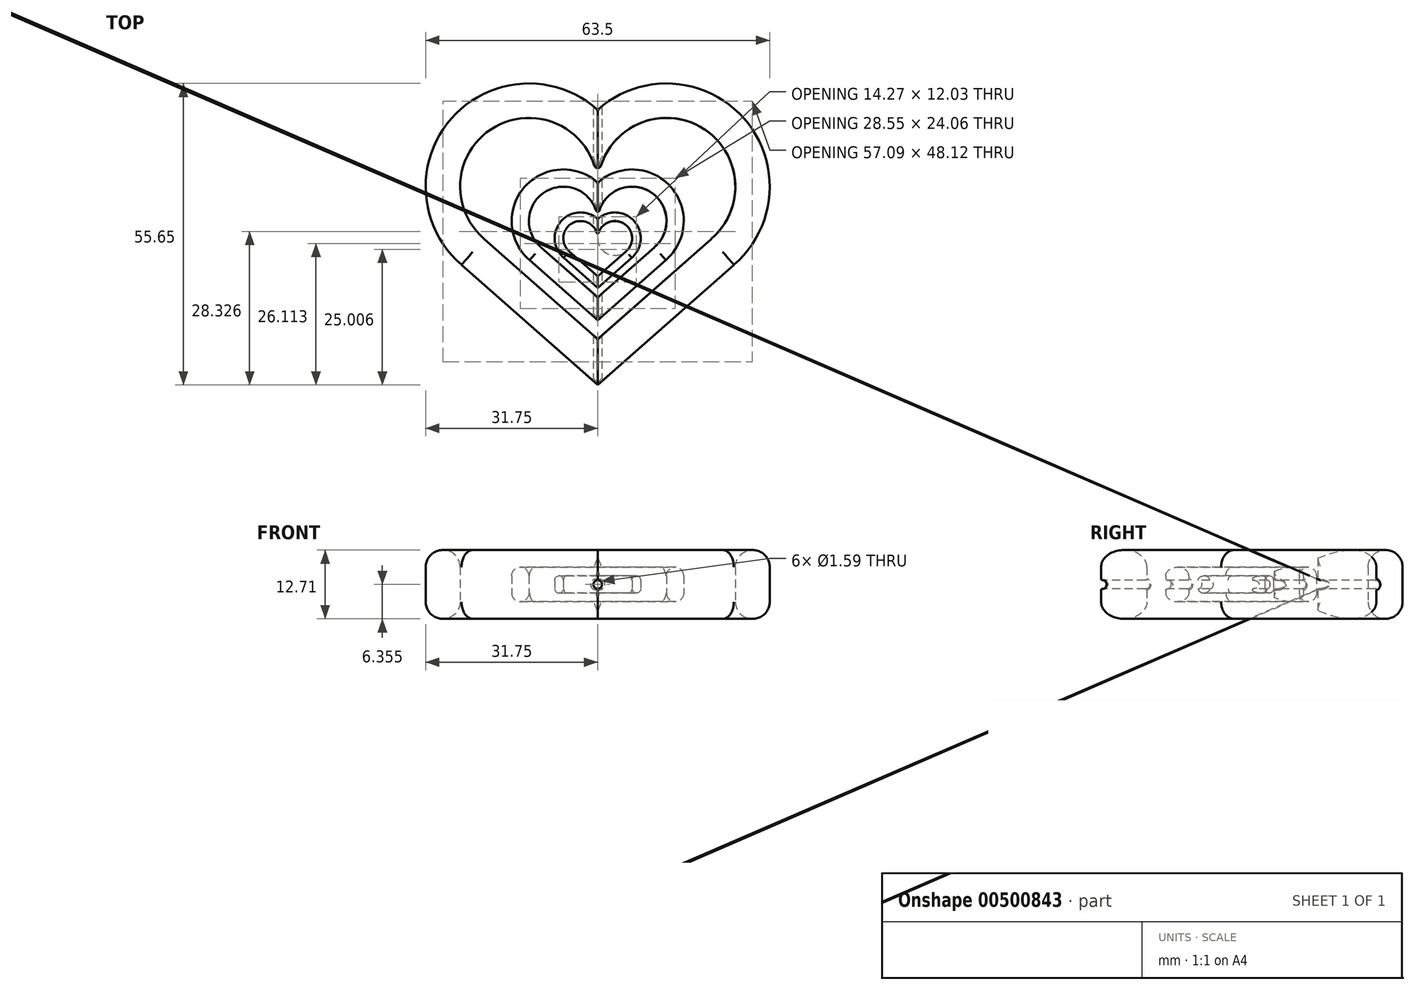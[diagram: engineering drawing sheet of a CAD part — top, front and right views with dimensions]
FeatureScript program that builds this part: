
annotation { "Feature Type Name" : "Feature", "Feature Type Description" : "" }
export const myFeature = defineFeature(function(context is Context, id is Id, definition is map)
    precondition{}
    {
        {
            var Q0;
            Q0=qCreatedBy(makeId("Top.planeOp"),FACE);
            var sketch = newSketch(context, id + "F0", { "sketchPlane" : qUnion([Q0])});
            skArc(sketch, "E0", {"start": v(0, 7.1) * mm, "mid": v(-13.5, 6.29) * mm, "end": v(-12.57, -7.21) * mm});
            skArc(sketch, "E1", {"start": v(0, 7.1) * mm, "mid": v(13.5, 6.29) * mm, "end": v(12.57, -7.21) * mm});
            skLineSegment(sketch, "E2", {"start": v(-12.57, -7.21) * mm, "end": v(0, -18.3) * mm});
            skLineSegment(sketch, "E3", {"start": v(0, -18.3) * mm, "end": v(12.57, -7.21) * mm});
            skArc(sketch, "E4", {"start": v(0, 0) * mm, "mid": v(-9, 5.77) * mm, "end": v(-10.5, -4.8) * mm});
            skArc(sketch, "E5", {"start": v(0, 0) * mm, "mid": v(9, 5.77) * mm, "end": v(10.49, -4.82) * mm});
            skLineSegment(sketch, "E6", {"start": v(10.49, -4.82) * mm, "end": v(0, -14.07) * mm});
            skLineSegment(sketch, "E7", {"start": v(0, -14.07) * mm, "end": v(-10.47, -4.83) * mm});
            skLineSegment(sketch, "E8", {"start": v(-10.47, -4.83) * mm, "end": v(-10.5, -4.8) * mm});
            skSolve(sketch);
        }
        {
            var Q0;
            Q0=makeQuery(id+"F0.imprint","IMPRINT",FACE,{"disambiguationData":[TD([[makeQuery(id+"F0.imprint","IMPRINT",EDGE,{"derivedFrom":sQuery(id+"F0.wireOp",EDGE,"E0")}),1.0]])]});
            extrude(context, id + "F1", {"entities" : qUnion([Q0]), "depth" : 6.35 * mm});
        }
        {
            var Q0;
            Q0=makeQuery(id+"F1.opExtrude","CAP_FACE",FACE,{"disambiguationData":[OSD([sQuery(id+"F0.wireOp",EDGE,"E0"),sQuery(id+"F0.wireOp",EDGE,"E1"),sQuery(id+"F0.wireOp",EDGE,"E2"),sQuery(id+"F0.wireOp",EDGE,"E3")])],"isStart":false});
            var Q1;
            Q1=makeQuery(id+"F1.opExtrude","CAP_FACE",FACE,{"disambiguationData":[OSD([sQuery(id+"F0.wireOp",EDGE,"E0"),sQuery(id+"F0.wireOp",EDGE,"E1"),sQuery(id+"F0.wireOp",EDGE,"E2"),sQuery(id+"F0.wireOp",EDGE,"E3")])],"isStart":true});
            fillet(context, id + "F2", {"entities" : qUnion([Q0, Q1]), "radius" : 1.57 * mm, "tangentPropagation" : true, "allowEdgeOverflow" : false});
        }
        {
            var Q0;
            Q0=makeQuery(id+"F2.opFillet","BLEND_EDGE",EDGE,{"blendedFrom":[makeQuery(id+"F1.opExtrude","CAP_EDGE",EDGE,{"disambiguationData":[OSD([sQuery(id+"F0.wireOp",EDGE,"E0")])],"isStart":false}),makeQuery(id+"F1.opExtrude","CAP_EDGE",EDGE,{"disambiguationData":[OSD([sQuery(id+"F0.wireOp",EDGE,"E2")])],"isStart":false})],"blendedInto":[]});
            var Q1;
            Q1=makeQuery(id+"F2.opFillet","BLEND_EDGE",EDGE,{"blendedFrom":[makeQuery(id+"F1.opExtrude","CAP_EDGE",EDGE,{"disambiguationData":[OSD([sQuery(id+"F0.wireOp",EDGE,"E1")])],"isStart":false}),makeQuery(id+"F1.opExtrude","CAP_EDGE",EDGE,{"disambiguationData":[OSD([sQuery(id+"F0.wireOp",EDGE,"E3")])],"isStart":false})],"blendedInto":[]});
            var Q2;
            Q2=makeQuery(id+"F1.opExtrude","SWEPT_EDGE",EDGE,{"disambiguationData":[OSD([sQuery(id+"F0.wireOp",EDGE,"E0"),sQuery(id+"F0.wireOp",EDGE,"E2")])]});
            var Q3;
            Q3=makeQuery(id+"F1.opExtrude","SWEPT_EDGE",EDGE,{"disambiguationData":[OSD([sQuery(id+"F0.wireOp",EDGE,"E1"),sQuery(id+"F0.wireOp",EDGE,"E3")])]});
            var Q4;
            Q4=makeQuery(id+"F2.opFillet","BLEND_EDGE",EDGE,{"blendedFrom":[makeQuery(id+"F1.opExtrude","CAP_EDGE",EDGE,{"disambiguationData":[OSD([sQuery(id+"F0.wireOp",EDGE,"E0")])],"isStart":true}),makeQuery(id+"F1.opExtrude","CAP_EDGE",EDGE,{"disambiguationData":[OSD([sQuery(id+"F0.wireOp",EDGE,"E2")])],"isStart":true})],"blendedInto":[]});
            var Q5;
            Q5=makeQuery(id+"F2.opFillet","BLEND_EDGE",EDGE,{"blendedFrom":[makeQuery(id+"F1.opExtrude","CAP_EDGE",EDGE,{"disambiguationData":[OSD([sQuery(id+"F0.wireOp",EDGE,"E1")])],"isStart":true}),makeQuery(id+"F1.opExtrude","CAP_EDGE",EDGE,{"disambiguationData":[OSD([sQuery(id+"F0.wireOp",EDGE,"E3")])],"isStart":true})],"blendedInto":[]});
            var Q6;
            Q6=makeQuery(id+"F2.opFillet","BLEND_EDGE",EDGE,{"blendedFrom":[makeQuery(id+"F1.opExtrude","CAP_EDGE",EDGE,{"disambiguationData":[OSD([sQuery(id+"F0.wireOp",EDGE,"E5")])],"isStart":false}),makeQuery(id+"F1.opExtrude","CAP_EDGE",EDGE,{"disambiguationData":[OSD([sQuery(id+"F0.wireOp",EDGE,"E6")])],"isStart":false})],"blendedInto":[]});
            var Q7;
            Q7=makeQuery(id+"F2.opFillet","BLEND_EDGE",EDGE,{"blendedFrom":[makeQuery(id+"F1.opExtrude","CAP_EDGE",EDGE,{"disambiguationData":[OSD([sQuery(id+"F0.wireOp",EDGE,"E4")])],"isStart":false}),makeQuery(id+"F1.opExtrude","CAP_EDGE",EDGE,{"disambiguationData":[OSD([sQuery(id+"F0.wireOp",EDGE,"E8")])],"isStart":false})],"blendedInto":[]});
            var Q8;
            Q8=makeQuery(id+"F1.opExtrude","SWEPT_EDGE",EDGE,{"disambiguationData":[OSD([sQuery(id+"F0.wireOp",EDGE,"E5"),sQuery(id+"F0.wireOp",EDGE,"E6")])]});
            var Q9;
            Q9=makeQuery(id+"F2.opFillet","BLEND_EDGE",EDGE,{"blendedFrom":[makeQuery(id+"F1.opExtrude","CAP_EDGE",EDGE,{"disambiguationData":[OSD([sQuery(id+"F0.wireOp",EDGE,"E5")])],"isStart":true}),makeQuery(id+"F1.opExtrude","CAP_EDGE",EDGE,{"disambiguationData":[OSD([sQuery(id+"F0.wireOp",EDGE,"E6")])],"isStart":true})],"blendedInto":[]});
            var Q10;
            Q10=makeQuery(id+"F2.opFillet","BLEND_EDGE",EDGE,{"blendedFrom":[makeQuery(id+"F1.opExtrude","CAP_EDGE",EDGE,{"disambiguationData":[OSD([sQuery(id+"F0.wireOp",EDGE,"E7")])],"isStart":true}),makeQuery(id+"F1.opExtrude","CAP_EDGE",EDGE,{"disambiguationData":[OSD([sQuery(id+"F0.wireOp",EDGE,"E8")])],"isStart":true})],"blendedInto":[]});
            var Q11;
            Q11=makeQuery(id+"F1.opExtrude","SWEPT_EDGE",EDGE,{"disambiguationData":[OSD([sQuery(id+"F0.wireOp",EDGE,"E7"),sQuery(id+"F0.wireOp",EDGE,"E8")])]});
            fillet(context, id + "F3", {"entities" : qUnion([Q0, Q1, Q2, Q3, Q4, Q5, Q6, Q7, Q8, Q9, Q10, Q11]), "radius" : 2.54 * mm, "tangentPropagation" : true, "allowEdgeOverflow" : false});
        }
        {
            var Q0;
            Q0=makeQuery(id+"F1.opExtrude","SWEPT_EDGE",EDGE,{"disambiguationData":[OSD([sQuery(id+"F0.wireOp",EDGE,"E4"),sQuery(id+"F0.wireOp",EDGE,"E5")])]});
            fillet(context, id + "F4", {"entities" : qUnion([Q0]), "radius" : 0.32 * mm, "tangentPropagation" : true, "allowEdgeOverflow" : false});
        }
        {
            var Q0;
            Q0=makeQuery(id+"F1.opExtrude","SWEPT_BODY",BODY,{"disambiguationData":[OSD([sQuery(id+"F0.wireOp",EDGE,"E0"),sQuery(id+"F0.wireOp",EDGE,"E1"),sQuery(id+"F0.wireOp",EDGE,"E2"),sQuery(id+"F0.wireOp",EDGE,"E3"),sQuery(id+"F0.wireOp",EDGE,"E4"),sQuery(id+"F0.wireOp",EDGE,"E5"),sQuery(id+"F0.wireOp",EDGE,"E6"),sQuery(id+"F0.wireOp",EDGE,"E7"),sQuery(id+"F0.wireOp",EDGE,"E8")])]});
            transform(context, id + "F5", {"entities" : qUnion([Q0]), "transformType" : TransformType.COPY});
        }
        {
            var Q0;
            Q0=makeQuery(id+"F5.opPattern","COPY",BODY,{"derivedFrom":makeQuery(id+"F1.opExtrude","SWEPT_BODY",BODY,{"disambiguationData":[OSD([sQuery(id+"F0.wireOp",EDGE,"E0"),sQuery(id+"F0.wireOp",EDGE,"E1"),sQuery(id+"F0.wireOp",EDGE,"E2"),sQuery(id+"F0.wireOp",EDGE,"E3"),sQuery(id+"F0.wireOp",EDGE,"E4"),sQuery(id+"F0.wireOp",EDGE,"E5"),sQuery(id+"F0.wireOp",EDGE,"E6"),sQuery(id+"F0.wireOp",EDGE,"E7"),sQuery(id+"F0.wireOp",EDGE,"E8")])]}),"instanceName":"1"});
            var Q1;
            Q1=qCreatedBy(makeId("Origin.pointOp"),VERTEX);
            transform(context, id + "F6", {"entities" : qUnion([Q0]), "transformType" : TransformType.SCALE_UNIFORMLY, "scale" : .5, "scalePoint" : qUnion([Q1]), "makeCopy" : false});
        }
        {
            var Q0;
            Q0=makeQuery(id+"F5.opPattern","COPY",BODY,{"derivedFrom":makeQuery(id+"F1.opExtrude","SWEPT_BODY",BODY,{"disambiguationData":[OSD([sQuery(id+"F0.wireOp",EDGE,"E0"),sQuery(id+"F0.wireOp",EDGE,"E1"),sQuery(id+"F0.wireOp",EDGE,"E2"),sQuery(id+"F0.wireOp",EDGE,"E3"),sQuery(id+"F0.wireOp",EDGE,"E4"),sQuery(id+"F0.wireOp",EDGE,"E5"),sQuery(id+"F0.wireOp",EDGE,"E6"),sQuery(id+"F0.wireOp",EDGE,"E7"),sQuery(id+"F0.wireOp",EDGE,"E8")])]}),"instanceName":"1"});
            var Q1;
            Q1=qCreatedBy(makeId("Front.planeOp"),FACE);
            transform(context, id + "F7", {"entities" : qUnion([Q0]), "transformType" : TransformType.TRANSLATION_DISTANCE, "transformDirection" : qUnion([Q1]), "distance" : 3.17 * mm, "makeCopy" : false});
        }
        {
            var Q0;
            Q0=makeQuery(id+"F5.opPattern","COPY",BODY,{"derivedFrom":makeQuery(id+"F1.opExtrude","SWEPT_BODY",BODY,{"disambiguationData":[OSD([sQuery(id+"F0.wireOp",EDGE,"E0"),sQuery(id+"F0.wireOp",EDGE,"E1"),sQuery(id+"F0.wireOp",EDGE,"E2"),sQuery(id+"F0.wireOp",EDGE,"E3"),sQuery(id+"F0.wireOp",EDGE,"E4"),sQuery(id+"F0.wireOp",EDGE,"E5"),sQuery(id+"F0.wireOp",EDGE,"E6"),sQuery(id+"F0.wireOp",EDGE,"E7"),sQuery(id+"F0.wireOp",EDGE,"E8")])]}),"instanceName":"1"});
            var Q1;
            Q1=qCreatedBy(makeId("Top.planeOp"),FACE);
            transform(context, id + "F8", {"entities" : qUnion([Q0]), "transformType" : TransformType.TRANSLATION_DISTANCE, "transformDirection" : qUnion([Q1]), "distance" : 1.59 * mm, "makeCopy" : false});
        }
        {
            var Q0;
            Q0=makeQuery(id+"F1.opExtrude","SWEPT_BODY",BODY,{"disambiguationData":[OSD([sQuery(id+"F0.wireOp",EDGE,"E0"),sQuery(id+"F0.wireOp",EDGE,"E1"),sQuery(id+"F0.wireOp",EDGE,"E2"),sQuery(id+"F0.wireOp",EDGE,"E3"),sQuery(id+"F0.wireOp",EDGE,"E4"),sQuery(id+"F0.wireOp",EDGE,"E5"),sQuery(id+"F0.wireOp",EDGE,"E6"),sQuery(id+"F0.wireOp",EDGE,"E7"),sQuery(id+"F0.wireOp",EDGE,"E8")])]});
            var Q1;
            Q1=qCreatedBy(makeId("Origin.pointOp"),VERTEX);
            transform(context, id + "F9", {"entities" : qUnion([Q0]), "transformType" : TransformType.SCALE_UNIFORMLY, "scale" : 2, "scalePoint" : qUnion([Q1]), "makeCopy" : true});
        }
        {
            var Q0;
            Q0=qCreatedBy(makeId("Front.planeOp"),FACE);
            var sketch = newSketch(context, id + "F10", { "sketchPlane" : qUnion([Q0])});
            skCircle(sketch, "E9", {"center": v(0, 3.18) * mm, "radius": 0.8 * mm});
            skSolve(sketch);
        }
        {
            var Q0;
            Q0=makeQuery(id+"F9.opPattern","COPY",BODY,{"derivedFrom":makeQuery(id+"F1.opExtrude","SWEPT_BODY",BODY,{"disambiguationData":[OSD([sQuery(id+"F0.wireOp",EDGE,"E0"),sQuery(id+"F0.wireOp",EDGE,"E1"),sQuery(id+"F0.wireOp",EDGE,"E2"),sQuery(id+"F0.wireOp",EDGE,"E3"),sQuery(id+"F0.wireOp",EDGE,"E4"),sQuery(id+"F0.wireOp",EDGE,"E5"),sQuery(id+"F0.wireOp",EDGE,"E6"),sQuery(id+"F0.wireOp",EDGE,"E7"),sQuery(id+"F0.wireOp",EDGE,"E8")])]}),"instanceName":"1"});
            var Q1;
            Q1=qCreatedBy(makeId("Front.planeOp"),FACE);
            transform(context, id + "F11", {"entities" : qUnion([Q0]), "transformType" : TransformType.TRANSLATION_DISTANCE, "transformDirection" : qUnion([Q1]), "distance" : 6.35 * mm, "oppositeDirection" : true, "makeCopy" : false});
        }
        {
            var Q0;
            Q0=makeQuery(id+"F9.opPattern","COPY",BODY,{"derivedFrom":makeQuery(id+"F1.opExtrude","SWEPT_BODY",BODY,{"disambiguationData":[OSD([sQuery(id+"F0.wireOp",EDGE,"E0"),sQuery(id+"F0.wireOp",EDGE,"E1"),sQuery(id+"F0.wireOp",EDGE,"E2"),sQuery(id+"F0.wireOp",EDGE,"E3"),sQuery(id+"F0.wireOp",EDGE,"E4"),sQuery(id+"F0.wireOp",EDGE,"E5"),sQuery(id+"F0.wireOp",EDGE,"E6"),sQuery(id+"F0.wireOp",EDGE,"E7"),sQuery(id+"F0.wireOp",EDGE,"E8")])]}),"instanceName":"1"});
            var Q1;
            Q1=qCreatedBy(makeId("Top.planeOp"),FACE);
            transform(context, id + "F12", {"entities" : qUnion([Q0]), "transformType" : TransformType.TRANSLATION_DISTANCE, "transformDirection" : qUnion([Q1]), "distance" : 3.17 * mm, "oppositeDirection" : true, "makeCopy" : false});
        }
        {
            var Q0;
            Q0 = qSketchRegion(id + "F10", true);
            extrude(context, id + "F13", {"entities" : qUnion([Q0]), "operationType" : NewBodyOperationType.REMOVE, "endBound" : BoundingType.SYMMETRIC, "oppositeDirection" : true, "depth" : 101.6 * mm});
        }
        {
            var Q0;
            Q0=makeQuery(id+"F13.boolean.opBoolean","COPY",FACE,{"disambiguationData":[TD([makeQuery(id+"F1.opExtrude","SWEPT_FACE",FACE,{"disambiguationData":[OSD([sQuery(id+"F0.wireOp",EDGE,"E2")])]})])],"derivedFrom":makeQuery(id+"F13.opExtrude","SWEPT_FACE",FACE,{"disambiguationData":[OSD([sQuery(id+"F10.wireOp",EDGE,"E9")])]})});
            var Q1;
            Q1=makeQuery(id+"F13.boolean.opBoolean","COPY",FACE,{"disambiguationData":[TD([makeQuery(id+"F5.opPattern","COPY",FACE,{"derivedFrom":makeQuery(id+"F1.opExtrude","SWEPT_FACE",FACE,{"disambiguationData":[OSD([sQuery(id+"F0.wireOp",EDGE,"E2")])]}),"instanceName":"1"})])],"derivedFrom":makeQuery(id+"F13.opExtrude","SWEPT_FACE",FACE,{"disambiguationData":[OSD([sQuery(id+"F10.wireOp",EDGE,"E9")])]})});
            var Q2;
            Q2=makeQuery(id+"F13.boolean.opBoolean","COPY",FACE,{"disambiguationData":[TD([makeQuery(id+"F5.opPattern","COPY",FACE,{"derivedFrom":makeQuery(id+"F1.opExtrude","SWEPT_FACE",FACE,{"disambiguationData":[OSD([sQuery(id+"F0.wireOp",EDGE,"E0")])]}),"instanceName":"1"})])],"derivedFrom":makeQuery(id+"F13.opExtrude","SWEPT_FACE",FACE,{"disambiguationData":[OSD([sQuery(id+"F10.wireOp",EDGE,"E9")])]})});
            var Q3;
            Q3=makeQuery(id+"F13.boolean.opBoolean","COPY",FACE,{"disambiguationData":[TD([makeQuery(id+"F1.opExtrude","SWEPT_FACE",FACE,{"disambiguationData":[OSD([sQuery(id+"F0.wireOp",EDGE,"E0")])]})])],"derivedFrom":makeQuery(id+"F13.opExtrude","SWEPT_FACE",FACE,{"disambiguationData":[OSD([sQuery(id+"F10.wireOp",EDGE,"E9")])]})});
            var Q4;
            Q4=makeQuery(id+"F13.boolean.opBoolean","COPY",FACE,{"disambiguationData":[TD([makeQuery(id+"F9.opPattern","COPY",FACE,{"derivedFrom":makeQuery(id+"F1.opExtrude","SWEPT_FACE",FACE,{"disambiguationData":[OSD([sQuery(id+"F0.wireOp",EDGE,"E2")])]}),"instanceName":"1"})])],"derivedFrom":makeQuery(id+"F13.opExtrude","SWEPT_FACE",FACE,{"disambiguationData":[OSD([sQuery(id+"F10.wireOp",EDGE,"E9")])]})});
            var Q5;
            Q5=makeQuery(id+"F13.boolean.opBoolean","COPY",FACE,{"disambiguationData":[TD([makeQuery(id+"F9.opPattern","COPY",FACE,{"derivedFrom":makeQuery(id+"F1.opExtrude","SWEPT_FACE",FACE,{"disambiguationData":[OSD([sQuery(id+"F0.wireOp",EDGE,"E0")])]}),"instanceName":"1"})])],"derivedFrom":makeQuery(id+"F13.opExtrude","SWEPT_FACE",FACE,{"disambiguationData":[OSD([sQuery(id+"F10.wireOp",EDGE,"E9")])]})});
            fillet(context, id + "F14", {"entities" : qUnion([Q0, Q1, Q2, Q3, Q4, Q5]), "radius" : 0.25 * mm, "tangentPropagation" : true, "allowEdgeOverflow" : false});
        }
    });
